# Revit family: 1402a_omni_bp_us
name_source: partatom
category: Communication Devices
units: mm (PartAtom-declared; Revit-internal decimal feet)

## family parameters
Cut with Voids When Loaded = No
Host = Face
Maintain Annotation Orientation = No
OmniClass Number = 23.85.80.11.27
OmniClass Title = Lighting Controls
Part Type = Normal
Room Calculation Point = No
Round Connector Dimension = Use Diameter
Shared = Yes

## types (1)
- 1402a_omni_bp_us
    Assembly Code = D5090
    Certifications = UL and cUL listed
    Coverage = 500 - 2000 sq ft, based on model
    Default Elevation = 48 "
    Description = The OMNIUSBP1277 line voltage ceiling sensor uses ultrasonic (US) technology to
turn lighting on and off based on occupancy. Designed specifically for both areas
with obstructions (e.g. columns, cubicles, stalls, and filing cabinets) and areas with
long periods of minor-motion activity (e.g. typing), this sensor features 
Controls' patented IntelliDAPT® technology, which makes all the sensor
adjustments automatically.
    Features = IntelliDAPT self-adaptive technology — no manual adjustment required 
Superior all-digital ultrasonic (US) minor motion detection 
Non-volatile memory for sensor settings
500–2,000 square-foot coverage area (depending on model)
Self-contained power supply
Universal voltage (120-277VAC; 50/60 Hz)
UL and cUL listed 
California Title 24 compliant 
Five-year warranty 
120-277 Vac
    Housing Material = Paint -  Matte White
    Manufacturer = NX Lighting Controls
    Model = OMNI®-BP Line Voltage Ultrasonic Ceiling Sensor
    Power Requirements = 120-277VAC; 50/60Hz
    Sensing Element = Metal-Galvanized_Steel
    Type Comments = OMNI® Low Voltage Dual Technology Ultrasonic and PIR
    URL = https://www.currentlighting.com
    Warranty = 5-Years Warranty
    Width = 4.5 "

## geometry (parser evidence)
native form markers: Sweep x2
no freeform markers — native parametric forms only
